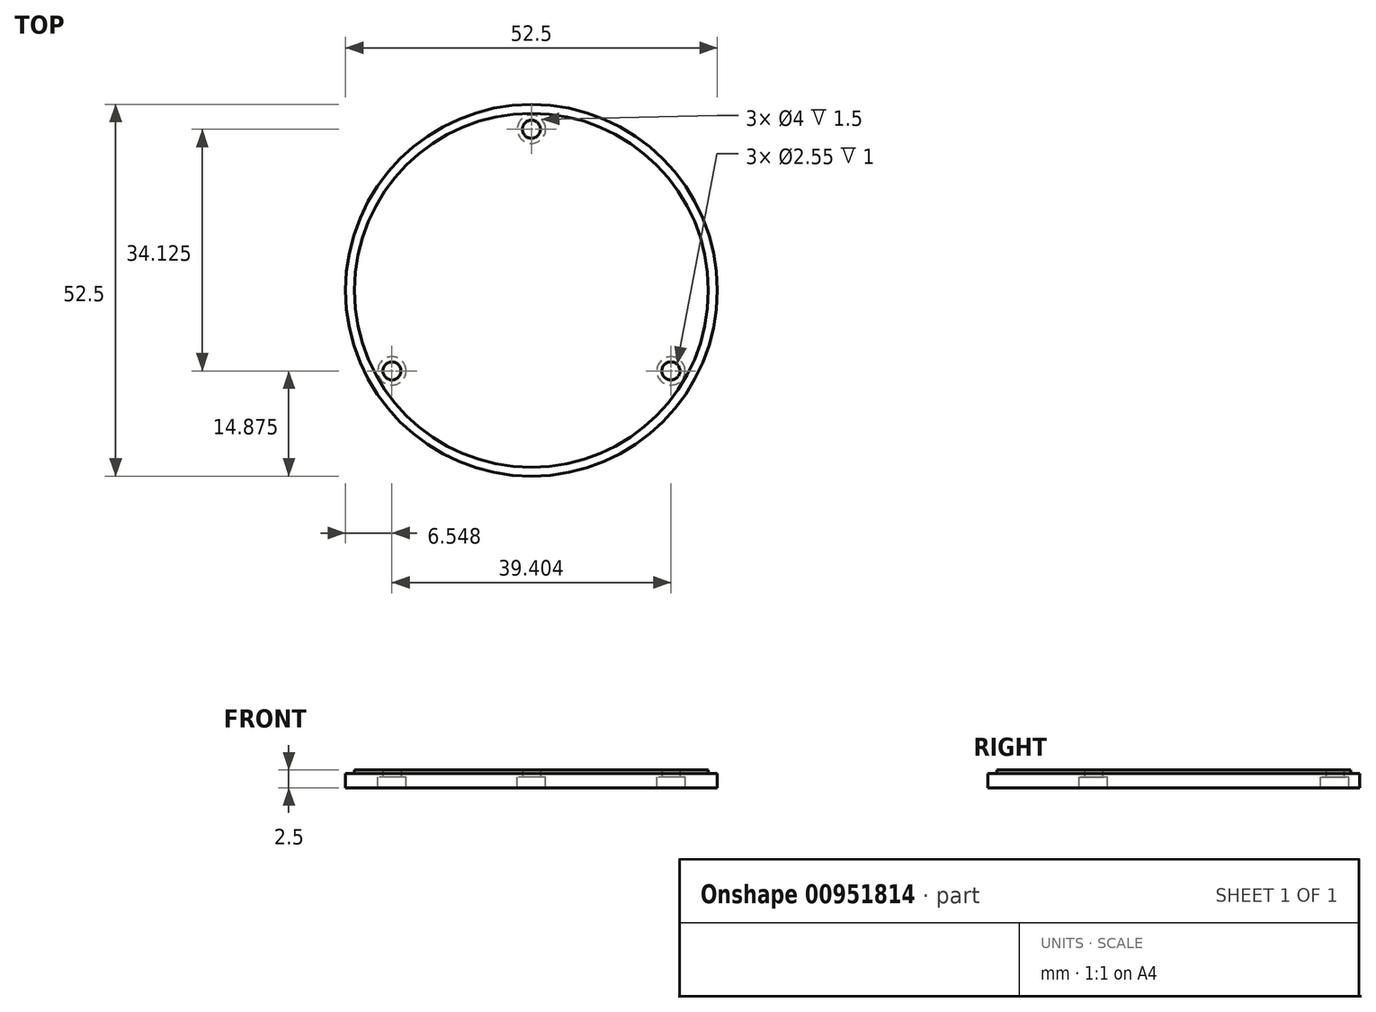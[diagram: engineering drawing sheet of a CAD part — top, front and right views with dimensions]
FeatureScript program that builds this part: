
annotation { "Feature Type Name" : "Feature", "Feature Type Description" : "" }
export const myFeature = defineFeature(function(context is Context, id is Id, definition is map)
    precondition{}
    {
        {
            var Q0;
            Q0=qCreatedBy(makeId("Top.planeOp"),FACE);
            var sketch = newSketch(context, id + "F0", { "sketchPlane" : qUnion([Q0])});
            skCircle(sketch, "E0", {"center": v(0, 0) * mm, "radius": 26.25 * mm});
            skCircle(sketch, "E1", {"center": v(0, 0) * mm, "radius": 22.75 * mm});
            skCircle(sketch, "E2", {"center": v(0, 0) * mm, "radius": 25 * mm});
            skCircle(sketch, "E3", {"center": v(0, 22.75) * mm, "radius": 1.27 * mm});
            skCircle(sketch, "E4", {"center": v(0, 22.75) * mm, "radius": 2 * mm});
            skCircle(sketch, "E5.1.0", {"center": v(-19.7, -11.37) * mm, "radius": 1.27 * mm});
            skCircle(sketch, "E5.1.1", {"center": v(-19.7, -11.37) * mm, "radius": 2 * mm});
            skCircle(sketch, "E5.2.0", {"center": v(19.7, -11.38) * mm, "radius": 1.27 * mm});
            skCircle(sketch, "E5.2.1", {"center": v(19.7, -11.38) * mm, "radius": 2 * mm});
            skLineSegment(sketch, "E5.anchor1", {"start": v(0, 0) * mm, "end": v(0, 22.75) * mm, "construction": true});
            skLineSegment(sketch, "E5.anchor2", {"start": v(0, 0) * mm, "end": v(19.7, -11.38) * mm, "construction": true});
            skSolve(sketch);
        }
        {
            var Q0;
            {var subQ0=sQuery(id+"F0.wireOp",EDGE,"E5.1.1");var subQ1=sQuery(id+"F0.wireOp",EDGE,"E1");var subQ2=makeQuery(id+"F0.imprint","INTERSECT",VERTEX,{"disambiguationData":[OD(0.0)],"derivedFrom":[subQ1,subQ0]});Q0=makeQuery(id+"F0.imprint","IMPRINT",FACE,{"disambiguationData":[TD([[makeQuery(id+"F0.imprint","IMPRINT",EDGE,{"disambiguationData":[TD([[subQ2,-1.0]])],"derivedFrom":subQ1}),1.0]])]});}
            var Q1;
            {var subQ0=sQuery(id+"F0.wireOp",EDGE,"E5.1.1");var subQ1=sQuery(id+"F0.wireOp",EDGE,"E1");var subQ2=makeQuery(id+"F0.imprint","INTERSECT",VERTEX,{"disambiguationData":[OD(0.0)],"derivedFrom":[subQ1,subQ0]});Q1=makeQuery(id+"F0.imprint","IMPRINT",FACE,{"disambiguationData":[TD([[makeQuery(id+"F0.imprint","IMPRINT",EDGE,{"disambiguationData":[TD([[subQ2,-1.0]])],"derivedFrom":subQ1}),-1.0]])]});}
            var Q2;
            Q2=makeQuery(id+"F0.imprint","IMPRINT",FACE,{"disambiguationData":[TD([[makeQuery(id+"F0.imprint","IMPRINT",EDGE,{"derivedFrom":sQuery(id+"F0.wireOp",EDGE,"E2")}),1.0]])]});
            var Q3;
            {var subQ0=sQuery(id+"F0.wireOp",EDGE,"E4");var subQ1=sQuery(id+"F0.wireOp",EDGE,"E1");var subQ3=makeQuery(id+"F0.imprint","INTERSECT",VERTEX,{"disambiguationData":[OD(1.0)],"derivedFrom":[subQ1,subQ0]});Q3=makeQuery(id+"F0.imprint","IMPRINT",FACE,{"disambiguationData":[TD([[makeQuery(id+"F0.imprint","IMPRINT",EDGE,{"disambiguationData":[TD([[subQ3,-1.0]])],"derivedFrom":subQ1}),1.0]])]});}
            var Q4;
            {var subQ0=sQuery(id+"F0.wireOp",EDGE,"E5.2.1");var subQ1=sQuery(id+"F0.wireOp",EDGE,"E1");var subQ2=makeQuery(id+"F0.imprint","INTERSECT",VERTEX,{"disambiguationData":[OD(0.0)],"derivedFrom":[subQ1,subQ0]});Q4=makeQuery(id+"F0.imprint","IMPRINT",FACE,{"disambiguationData":[TD([[makeQuery(id+"F0.imprint","IMPRINT",EDGE,{"disambiguationData":[TD([[subQ2,-1.0]])],"derivedFrom":subQ1}),1.0]])]});}
            var Q5;
            {var subQ0=sQuery(id+"F0.wireOp",EDGE,"E5.2.1");var subQ1=sQuery(id+"F0.wireOp",EDGE,"E1");var subQ2=makeQuery(id+"F0.imprint","INTERSECT",VERTEX,{"disambiguationData":[OD(0.0)],"derivedFrom":[subQ1,subQ0]});Q5=makeQuery(id+"F0.imprint","IMPRINT",FACE,{"disambiguationData":[TD([[makeQuery(id+"F0.imprint","IMPRINT",EDGE,{"disambiguationData":[TD([[subQ2,-1.0]])],"derivedFrom":subQ1}),-1.0]])]});}
            var Q6;
            {var subQ0=sQuery(id+"F0.wireOp",EDGE,"E3");var subQ1=sQuery(id+"F0.wireOp",EDGE,"E1");var subQ2=makeQuery(id+"F0.imprint","INTERSECT",VERTEX,{"disambiguationData":[OD(0.0)],"derivedFrom":[subQ1,subQ0]});Q6=makeQuery(id+"F0.imprint","IMPRINT",FACE,{"disambiguationData":[TD([[makeQuery(id+"F0.imprint","IMPRINT",EDGE,{"disambiguationData":[TD([[subQ2,1.0]])],"derivedFrom":subQ1}),-1.0]])]});}
            var Q7;
            {var subQ0=sQuery(id+"F0.wireOp",EDGE,"E3");var subQ1=sQuery(id+"F0.wireOp",EDGE,"E1");var subQ2=makeQuery(id+"F0.imprint","INTERSECT",VERTEX,{"disambiguationData":[OD(0.0)],"derivedFrom":[subQ1,subQ0]});Q7=makeQuery(id+"F0.imprint","IMPRINT",FACE,{"disambiguationData":[TD([[makeQuery(id+"F0.imprint","IMPRINT",EDGE,{"disambiguationData":[TD([[subQ2,1.0]])],"derivedFrom":subQ1}),1.0]])]});}
            extrude(context, id + "F1", {"entities" : qUnion([Q0, Q1, Q2, Q3, Q4, Q5, Q6, Q7]), "depth" : 0.5 * mm, "offsetDistance" : 25 * mm});
        }
        {
            var Q0;
            {var subQ0=sQuery(id+"F0.wireOp",EDGE,"E4");var subQ1=sQuery(id+"F0.wireOp",EDGE,"E1");var subQ3=makeQuery(id+"F0.imprint","INTERSECT",VERTEX,{"disambiguationData":[OD(1.0)],"derivedFrom":[subQ1,subQ0]});Q0=makeQuery(id+"F0.imprint","IMPRINT",FACE,{"disambiguationData":[TD([[makeQuery(id+"F0.imprint","IMPRINT",EDGE,{"disambiguationData":[TD([[subQ3,-1.0]])],"derivedFrom":subQ1}),1.0]])]});}
            var Q1;
            Q1=makeQuery(id+"F0.imprint","IMPRINT",FACE,{"disambiguationData":[TD([[makeQuery(id+"F0.imprint","IMPRINT",EDGE,{"derivedFrom":sQuery(id+"F0.wireOp",EDGE,"E2")}),1.0]])]});
            var Q2;
            Q2=makeQuery(id+"F0.imprint","IMPRINT",FACE,{"disambiguationData":[TD([[makeQuery(id+"F0.imprint","IMPRINT",EDGE,{"derivedFrom":sQuery(id+"F0.wireOp",EDGE,"E0")}),1.0]])]});
            extrude(context, id + "F2", {"entities" : qUnion([Q0, Q1, Q2]), "operationType" : NewBodyOperationType.ADD, "oppositeDirection" : true, "depth" : 2 * mm, "offsetDistance" : 25 * mm});
        }
        {
            var Q0;
            {var subQ0=sQuery(id+"F0.wireOp",EDGE,"E3");var subQ1=sQuery(id+"F0.wireOp",EDGE,"E1");var subQ2=makeQuery(id+"F0.imprint","INTERSECT",VERTEX,{"disambiguationData":[OD(0.0)],"derivedFrom":[subQ1,subQ0]});Q0=makeQuery(id+"F0.imprint","IMPRINT",FACE,{"disambiguationData":[TD([[makeQuery(id+"F0.imprint","IMPRINT",EDGE,{"disambiguationData":[TD([[subQ2,1.0]])],"derivedFrom":subQ1}),-1.0]])]});}
            var Q1;
            {var subQ0=sQuery(id+"F0.wireOp",EDGE,"E3");var subQ1=sQuery(id+"F0.wireOp",EDGE,"E1");var subQ2=makeQuery(id+"F0.imprint","INTERSECT",VERTEX,{"disambiguationData":[OD(0.0)],"derivedFrom":[subQ1,subQ0]});Q1=makeQuery(id+"F0.imprint","IMPRINT",FACE,{"disambiguationData":[TD([[makeQuery(id+"F0.imprint","IMPRINT",EDGE,{"disambiguationData":[TD([[subQ2,1.0]])],"derivedFrom":subQ1}),1.0]])]});}
            var Q2;
            {var subQ0=sQuery(id+"F0.wireOp",EDGE,"E5.1.1");var subQ1=sQuery(id+"F0.wireOp",EDGE,"E1");var subQ2=makeQuery(id+"F0.imprint","INTERSECT",VERTEX,{"disambiguationData":[OD(0.0)],"derivedFrom":[subQ1,subQ0]});Q2=makeQuery(id+"F0.imprint","IMPRINT",FACE,{"disambiguationData":[TD([[makeQuery(id+"F0.imprint","IMPRINT",EDGE,{"disambiguationData":[TD([[subQ2,-1.0]])],"derivedFrom":subQ1}),-1.0]])]});}
            var Q3;
            {var subQ0=sQuery(id+"F0.wireOp",EDGE,"E5.1.1");var subQ1=sQuery(id+"F0.wireOp",EDGE,"E1");var subQ2=makeQuery(id+"F0.imprint","INTERSECT",VERTEX,{"disambiguationData":[OD(0.0)],"derivedFrom":[subQ1,subQ0]});Q3=makeQuery(id+"F0.imprint","IMPRINT",FACE,{"disambiguationData":[TD([[makeQuery(id+"F0.imprint","IMPRINT",EDGE,{"disambiguationData":[TD([[subQ2,-1.0]])],"derivedFrom":subQ1}),1.0]])]});}
            var Q4;
            {var subQ0=sQuery(id+"F0.wireOp",EDGE,"E5.2.1");var subQ1=sQuery(id+"F0.wireOp",EDGE,"E1");var subQ2=makeQuery(id+"F0.imprint","INTERSECT",VERTEX,{"disambiguationData":[OD(0.0)],"derivedFrom":[subQ1,subQ0]});Q4=makeQuery(id+"F0.imprint","IMPRINT",FACE,{"disambiguationData":[TD([[makeQuery(id+"F0.imprint","IMPRINT",EDGE,{"disambiguationData":[TD([[subQ2,-1.0]])],"derivedFrom":subQ1}),1.0]])]});}
            var Q5;
            {var subQ0=sQuery(id+"F0.wireOp",EDGE,"E5.2.1");var subQ1=sQuery(id+"F0.wireOp",EDGE,"E1");var subQ2=makeQuery(id+"F0.imprint","INTERSECT",VERTEX,{"disambiguationData":[OD(0.0)],"derivedFrom":[subQ1,subQ0]});Q5=makeQuery(id+"F0.imprint","IMPRINT",FACE,{"disambiguationData":[TD([[makeQuery(id+"F0.imprint","IMPRINT",EDGE,{"disambiguationData":[TD([[subQ2,-1.0]])],"derivedFrom":subQ1}),-1.0]])]});}
            extrude(context, id + "F3", {"entities" : qUnion([Q0, Q1, Q2, Q3, Q4, Q5]), "operationType" : NewBodyOperationType.ADD, "oppositeDirection" : true, "depth" : 0.5 * mm, "offsetDistance" : 25 * mm});
        }
    });
